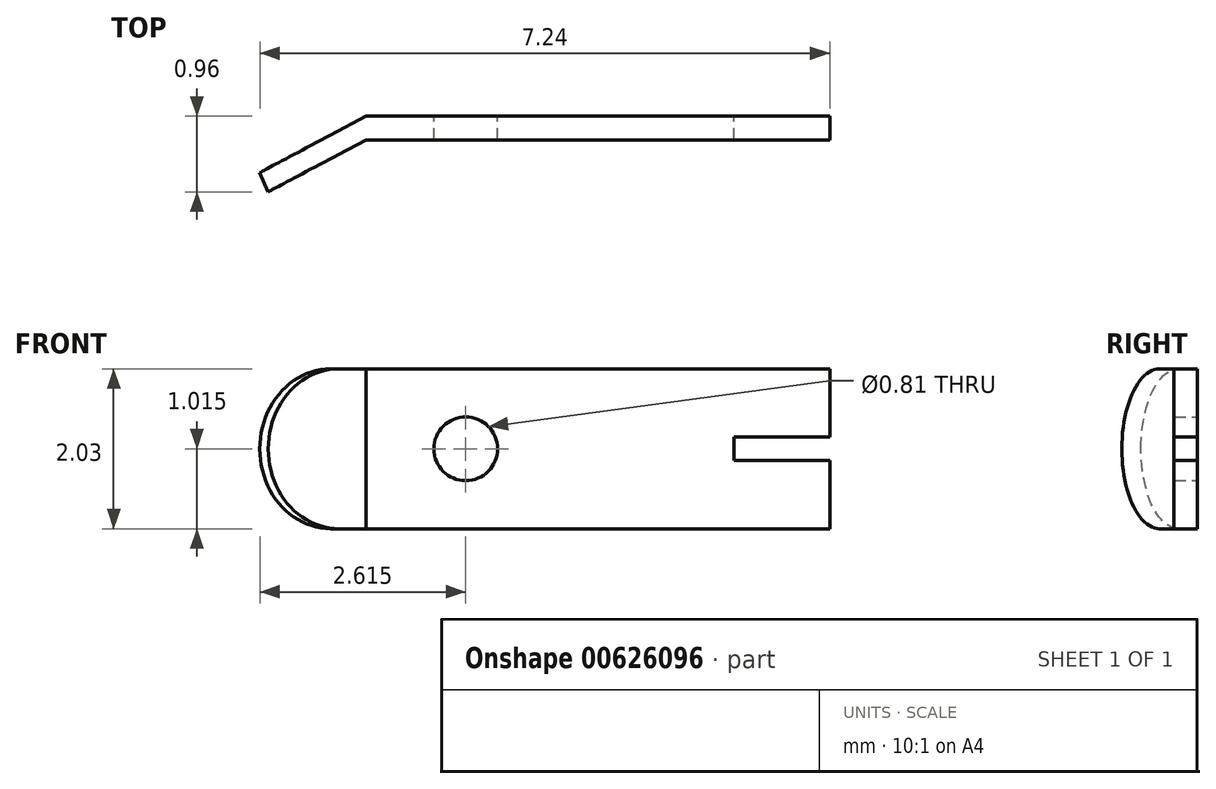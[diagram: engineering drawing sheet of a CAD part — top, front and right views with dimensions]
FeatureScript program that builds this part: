
annotation { "Feature Type Name" : "Feature", "Feature Type Description" : "" }
export const myFeature = defineFeature(function(context is Context, id is Id, definition is map)
    precondition{}
    {
        {
            var Q0;
            Q0=qCreatedBy(makeId("Front.planeOp"),FACE);
            var sketch = newSketch(context, id + "F0", { "sketchPlane" : qUnion([Q0])});
            skLineSegment(sketch, "E0.bottom", {"start": v(0, 0) * mm, "end": v(5.9, 0) * mm});
            skLineSegment(sketch, "E0.top", {"start": v(0, 2.03) * mm, "end": v(5.9, 2.03) * mm});
            skLineSegment(sketch, "E0.left", {"start": v(0, 0) * mm, "end": v(0, 2.03) * mm});
            skLineSegment(sketch, "E0.right", {"start": v(5.9, 0) * mm, "end": v(5.9, 2.03) * mm});
            skLineSegment(sketch, "E1.bottom", {"start": v(4.67, 0.87) * mm, "end": v(7.11, 0.87) * mm});
            skLineSegment(sketch, "E1.top", {"start": v(4.67, 1.17) * mm, "end": v(7.11, 1.17) * mm});
            skLineSegment(sketch, "E1.left", {"start": v(4.67, 0.87) * mm, "end": v(4.67, 1.16) * mm});
            skLineSegment(sketch, "E1.right", {"start": v(7.11, 0.87) * mm, "end": v(7.11, 1.17) * mm});
            skPoint(sketch, "E1.middle", {"position": v(5.9, 1.02) * mm});
            skPoint(sketch, "E2.centerSnap0", {"position": v(4.67, 1.02) * mm});
            skCircle(sketch, "E3", {"center": v(1.27, 1.01) * mm, "radius": 0.4 * mm});
            skSolve(sketch);
        }
        {
            var Q0;
            {var subQ1=sQuery(id+"F0.wireOp",EDGE,"E0.bottom");Q0=makeQuery(id+"F0.imprint","IMPRINT",FACE,{"disambiguationData":[TD([[makeQuery(id+"F0.imprint","IMPRINT",EDGE,{"derivedFrom":subQ1}),1.0]])]});}
            extrude(context, id + "F1", {"entities" : qUnion([Q0]), "depth" : 0.3 * mm, "offsetDistance" : 25 * mm});
        }
        {
            var Q0;
            Q0=makeQuery(id+"F1.opExtrude","SWEPT_FACE",FACE,{"disambiguationData":[OSD([sQuery(id+"F0.wireOp",EDGE,"E0.top")])]});
            var sketch = newSketch(context, id + "F2", { "sketchPlane" : qUnion([Q0])});
            skLineSegment(sketch, "E4", {"start": v(0, 0) * mm, "end": v(-1.35, -0.72) * mm});
            skLineSegment(sketch, "E5", {"start": v(0, -0.3) * mm, "end": v(0, 0) * mm});
            skLineSegment(sketch, "E6", {"start": v(0, -0.3) * mm, "end": v(-1.25, -0.96) * mm});
            skLineSegment(sketch, "E7", {"start": v(-1.25, -0.96) * mm, "end": v(-1.35, -0.72) * mm});
            skSolve(sketch);
        }
        {
            var Q0;
            Q0=makeQuery(id+"F2.imprint","IMPRINT",FACE,{"disambiguationData":[TD([[makeQuery(id+"F2.imprint","IMPRINT",EDGE,{"derivedFrom":sQuery(id+"F2.wireOp",EDGE,"E4")}),1.0]])]});
            extrude(context, id + "F3", {"entities" : qUnion([Q0]), "operationType" : NewBodyOperationType.ADD, "oppositeDirection" : true, "depth" : 2.03 * mm, "offsetDistance" : 25 * mm});
        }
        {
            var Q0;
            Q0=makeQuery(id+"F3.opExtrude","CAP_EDGE",EDGE,{"disambiguationData":[OSD([sQuery(id+"F2.wireOp",EDGE,"E7")])],"isStart":false});
            var Q1;
            Q1=makeQuery(id+"F3.opExtrude","CAP_EDGE",EDGE,{"disambiguationData":[OSD([sQuery(id+"F2.wireOp",EDGE,"E7")])],"isStart":true});
            fillet(context, id + "F4", {"entities" : qUnion([Q0, Q1]), "radius" : 1.01 * mm, "tangentPropagation" : true, "allowEdgeOverflow" : false});
        }
    });
